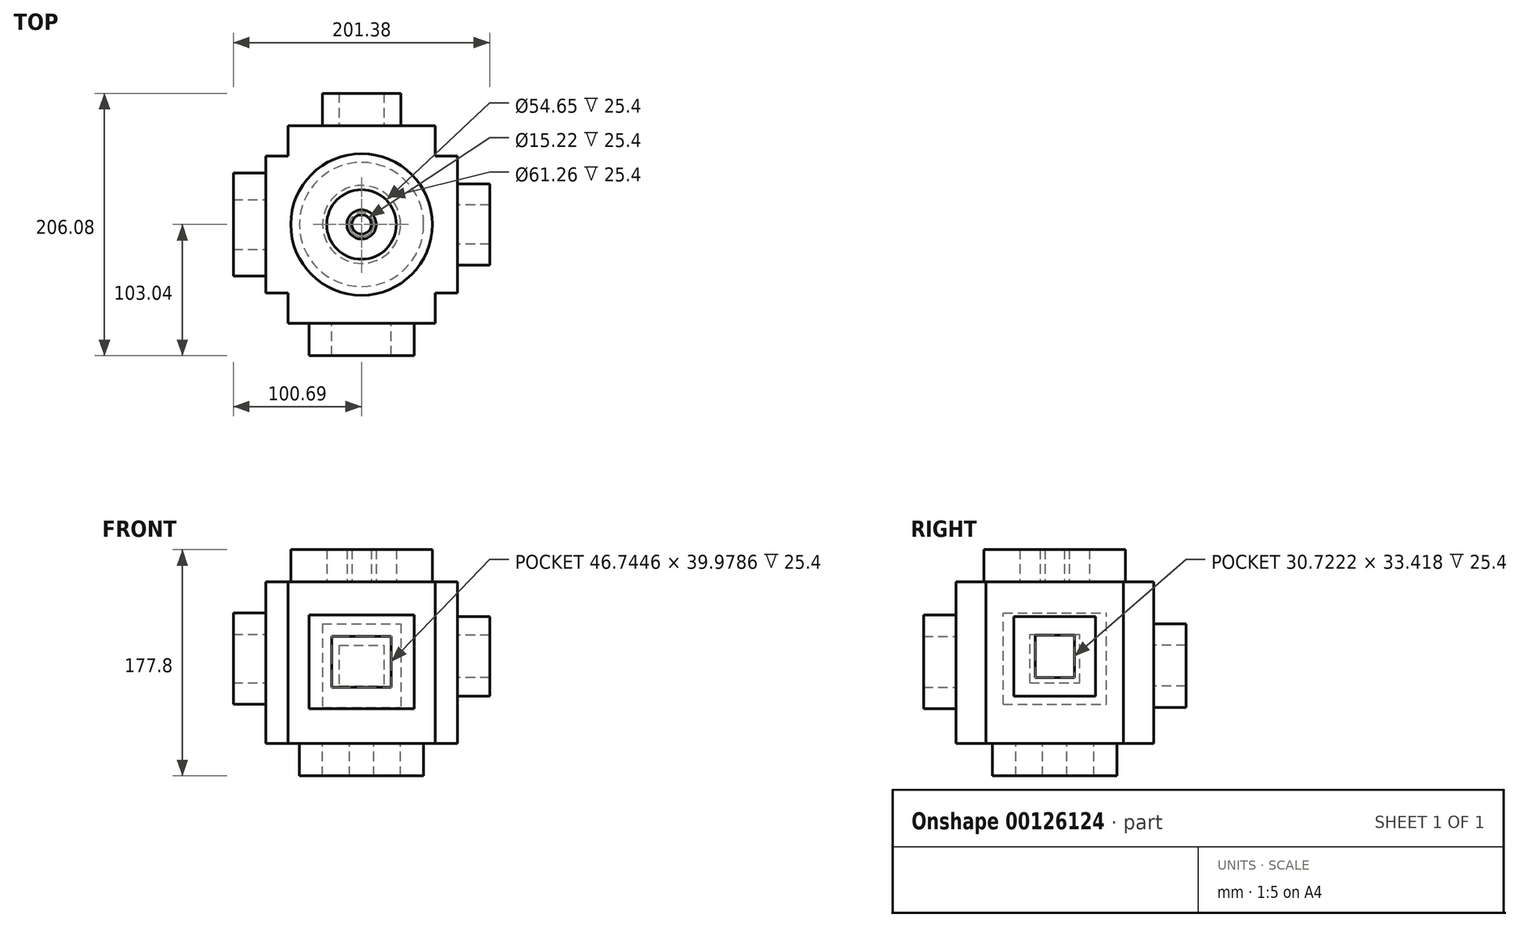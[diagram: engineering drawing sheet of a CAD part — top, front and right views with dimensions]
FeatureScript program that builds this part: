
annotation { "Feature Type Name" : "Feature", "Feature Type Description" : "" }
export const myFeature = defineFeature(function(context is Context, id is Id, definition is map)
    precondition{}
    {
        {
            var Q0;
            Q0=qCreatedBy(makeId("Top.planeOp"),FACE);
            var sketch = newSketch(context, id + "F0", { "sketchPlane" : qUnion([Q0])});
            skLineSegment(sketch, "E0.bottom", {"start": v(75.29, 53.92) * mm, "end": v(-75.29, 53.92) * mm});
            skLineSegment(sketch, "E0.top", {"start": v(75.29, -53.92) * mm, "end": v(-75.29, -53.92) * mm});
            skLineSegment(sketch, "E0.left", {"start": v(75.29, 53.92) * mm, "end": v(75.29, -53.92) * mm});
            skLineSegment(sketch, "E0.right", {"start": v(-75.29, 53.92) * mm, "end": v(-75.29, -53.92) * mm});
            skPoint(sketch, "E0.middle", {"position": v(0, 0) * mm});
            skLineSegment(sketch, "E1.bottom", {"start": v(57.75, 77.64) * mm, "end": v(-57.75, 77.64) * mm});
            skLineSegment(sketch, "E1.top", {"start": v(57.75, -77.64) * mm, "end": v(-57.75, -77.64) * mm});
            skLineSegment(sketch, "E1.left", {"start": v(57.75, 77.64) * mm, "end": v(57.75, -77.64) * mm});
            skLineSegment(sketch, "E1.right", {"start": v(-57.75, 77.64) * mm, "end": v(-57.75, -77.64) * mm});
            skSolve(sketch);
        }
        {
            var Q0;
            {var subQ0=sQuery(id+"F0.wireOp",EDGE,"E1.left");var subQ1=sQuery(id+"F0.wireOp",EDGE,"E0.bottom");var subQ2=makeQuery(id+"F0.imprint","INTERSECT",VERTEX,{"derivedFrom":[subQ1,subQ0]});Q0=makeQuery(id+"F0.imprint","IMPRINT",FACE,{"disambiguationData":[TD([[makeQuery(id+"F0.imprint","IMPRINT",EDGE,{"disambiguationData":[TD([[subQ2,-1.0]])],"derivedFrom":subQ1}),1.0]])]});}
            var Q1;
            {var subQ0=sQuery(id+"F0.wireOp",EDGE,"E0.right");Q1=makeQuery(id+"F0.imprint","IMPRINT",FACE,{"disambiguationData":[TD([[makeQuery(id+"F0.imprint","IMPRINT",EDGE,{"derivedFrom":subQ0}),1.0]])]});}
            var Q2;
            {var subQ5=sQuery(id+"F0.wireOp",EDGE,"E1.bottom");Q2=makeQuery(id+"F0.imprint","IMPRINT",FACE,{"disambiguationData":[TD([[makeQuery(id+"F0.imprint","IMPRINT",EDGE,{"derivedFrom":subQ5}),1.0]])]});}
            var Q3;
            {var subQ0=sQuery(id+"F0.wireOp",EDGE,"E0.left");Q3=makeQuery(id+"F0.imprint","IMPRINT",FACE,{"disambiguationData":[TD([[makeQuery(id+"F0.imprint","IMPRINT",EDGE,{"derivedFrom":subQ0}),-1.0]])]});}
            var Q4;
            {var subQ5=sQuery(id+"F0.wireOp",EDGE,"E1.top");Q4=makeQuery(id+"F0.imprint","IMPRINT",FACE,{"disambiguationData":[TD([[makeQuery(id+"F0.imprint","IMPRINT",EDGE,{"derivedFrom":subQ5}),-1.0]])]});}
            extrude(context, id + "F1", {"entities" : qUnion([Q0, Q1, Q2, Q3, Q4]), "depth" : 127 * mm});
        }
        {
            var Q0;
            Q0=makeQuery(id+"F1.opExtrude","CAP_FACE",FACE,{"disambiguationData":[OSD([sQuery(id+"F0.wireOp",EDGE,"E0.bottom"),sQuery(id+"F0.wireOp",EDGE,"E0.top"),sQuery(id+"F0.wireOp",EDGE,"E0.left"),sQuery(id+"F0.wireOp",EDGE,"E0.right"),sQuery(id+"F0.wireOp",EDGE,"E1.bottom"),sQuery(id+"F0.wireOp",EDGE,"E1.top"),sQuery(id+"F0.wireOp",EDGE,"E1.left"),sQuery(id+"F0.wireOp",EDGE,"E1.right")])],"isStart":false});
            var sketch = newSketch(context, id + "F2", { "sketchPlane" : qUnion([Q0])});
            skCircle(sketch, "E2", {"center": v(0, 0) * mm, "radius": 55.61 * mm});
            skCircle(sketch, "E3", {"center": v(0, 0) * mm, "radius": 60.45 * mm});
            skCircle(sketch, "E4", {"center": v(0, 0) * mm, "radius": 41.5 * mm});
            skCircle(sketch, "E5", {"center": v(0, 0) * mm, "radius": 27.33 * mm});
            skCircle(sketch, "E6", {"center": v(0, 0) * mm, "radius": 17.16 * mm});
            skCircle(sketch, "E7", {"center": v(0, 0) * mm, "radius": 11.49 * mm});
            skCircle(sketch, "E8", {"center": v(0, 0) * mm, "radius": 7.61 * mm});
            skSolve(sketch);
        }
        {
            var Q0;
            Q0=makeQuery(id+"F2.imprint","IMPRINT",FACE,{"disambiguationData":[TD([[makeQuery(id+"F2.imprint","IMPRINT",EDGE,{"derivedFrom":sQuery(id+"F2.wireOp",EDGE,"E2")}),1.0]])]});
            var Q1;
            Q1=makeQuery(id+"F2.imprint","IMPRINT",FACE,{"disambiguationData":[TD([[makeQuery(id+"F2.imprint","IMPRINT",EDGE,{"derivedFrom":sQuery(id+"F2.wireOp",EDGE,"E4")}),1.0]])]});
            var Q2;
            Q2=makeQuery(id+"F2.imprint","IMPRINT",FACE,{"disambiguationData":[TD([[makeQuery(id+"F2.imprint","IMPRINT",EDGE,{"derivedFrom":sQuery(id+"F2.wireOp",EDGE,"E7")}),1.0]])]});
            extrude(context, id + "F3", {"entities" : qUnion([Q0, Q1, Q2]), "operationType" : NewBodyOperationType.ADD, "depth" : 25.4 * mm});
        }
        {
            var Q0;
            Q0=makeQuery(id+"F1.opExtrude","SWEPT_FACE",FACE,{"disambiguationData":[OSD([sQuery(id+"F0.wireOp",EDGE,"E0.left")])]});
            var sketch = newSketch(context, id + "F4", { "sketchPlane" : qUnion([Q0])});
            skLineSegment(sketch, "E9.bottom", {"start": v(32.02, 37.27) * mm, "end": v(-32.02, 37.27) * mm});
            skLineSegment(sketch, "E9.top", {"start": v(32.02, 99.76) * mm, "end": v(-32.02, 99.76) * mm});
            skLineSegment(sketch, "E9.left", {"start": v(32.02, 37.27) * mm, "end": v(32.02, 99.76) * mm});
            skLineSegment(sketch, "E9.right", {"start": v(-32.02, 37.27) * mm, "end": v(-32.02, 99.76) * mm});
            skPoint(sketch, "E9.middle", {"position": v(0, 68.52) * mm});
            skLineSegment(sketch, "E10.bottom", {"start": v(15.36, 51.8) * mm, "end": v(-15.36, 51.8) * mm});
            skLineSegment(sketch, "E10.top", {"start": v(15.36, 85.23) * mm, "end": v(-15.36, 85.23) * mm});
            skLineSegment(sketch, "E10.left", {"start": v(15.36, 51.8) * mm, "end": v(15.36, 85.23) * mm});
            skLineSegment(sketch, "E10.right", {"start": v(-15.36, 51.8) * mm, "end": v(-15.36, 85.23) * mm});
            skSolve(sketch);
        }
        {
            var Q0;
            Q0=makeQuery(id+"F4.imprint","IMPRINT",FACE,{"disambiguationData":[TD([[makeQuery(id+"F4.imprint","IMPRINT",EDGE,{"derivedFrom":sQuery(id+"F4.wireOp",EDGE,"E9.bottom")}),-1.0]])]});
            extrude(context, id + "F5", {"entities" : qUnion([Q0]), "operationType" : NewBodyOperationType.ADD, "depth" : 25.4 * mm});
        }
        {
            var Q0;
            Q0=makeQuery(id+"F1.opExtrude","SWEPT_FACE",FACE,{"disambiguationData":[OSD([sQuery(id+"F0.wireOp",EDGE,"E1.bottom")])]});
            var sketch = newSketch(context, id + "F6", { "sketchPlane" : qUnion([Q0])});
            skLineSegment(sketch, "E11.bottom", {"start": v(30.84, 94.16) * mm, "end": v(-30.84, 94.16) * mm});
            skLineSegment(sketch, "E11.top", {"start": v(30.84, 28.22) * mm, "end": v(-30.84, 28.22) * mm});
            skLineSegment(sketch, "E11.left", {"start": v(30.84, 94.16) * mm, "end": v(30.84, 28.22) * mm});
            skLineSegment(sketch, "E11.right", {"start": v(-30.84, 94.16) * mm, "end": v(-30.84, 28.22) * mm});
            skPoint(sketch, "E11.middle", {"position": v(0, 61.2) * mm});
            skLineSegment(sketch, "E12.bottom", {"start": v(17.59, 77.27) * mm, "end": v(-17.59, 77.27) * mm});
            skLineSegment(sketch, "E12.top", {"start": v(17.59, 45.11) * mm, "end": v(-17.59, 45.11) * mm});
            skLineSegment(sketch, "E12.left", {"start": v(17.59, 77.27) * mm, "end": v(17.59, 45.11) * mm});
            skLineSegment(sketch, "E12.right", {"start": v(-17.59, 77.27) * mm, "end": v(-17.59, 45.11) * mm});
            skSolve(sketch);
        }
        {
            var Q0;
            Q0=makeQuery(id+"F6.imprint","IMPRINT",FACE,{"disambiguationData":[TD([[makeQuery(id+"F6.imprint","IMPRINT",EDGE,{"derivedFrom":sQuery(id+"F6.wireOp",EDGE,"E11.bottom")}),1.0]])]});
            extrude(context, id + "F7", {"entities" : qUnion([Q0]), "operationType" : NewBodyOperationType.ADD, "depth" : 25.4 * mm});
        }
        {
            var Q0;
            Q0=makeQuery(id+"F1.opExtrude","SWEPT_FACE",FACE,{"disambiguationData":[OSD([sQuery(id+"F0.wireOp",EDGE,"E1.top")])]});
            var sketch = newSketch(context, id + "F8", { "sketchPlane" : qUnion([Q0])});
            skLineSegment(sketch, "E13.bottom", {"start": v(41.33, 27.27) * mm, "end": v(-41.33, 27.27) * mm});
            skLineSegment(sketch, "E13.top", {"start": v(41.33, 100.92) * mm, "end": v(-41.33, 100.92) * mm});
            skLineSegment(sketch, "E13.left", {"start": v(41.33, 27.27) * mm, "end": v(41.33, 100.92) * mm});
            skLineSegment(sketch, "E13.right", {"start": v(-41.33, 27.27) * mm, "end": v(-41.33, 100.92) * mm});
            skPoint(sketch, "E13.middle", {"position": v(0, 64.1) * mm});
            skLineSegment(sketch, "E14.bottom", {"start": v(23.37, 44.1) * mm, "end": v(-23.37, 44.1) * mm});
            skLineSegment(sketch, "E14.top", {"start": v(23.37, 84.08) * mm, "end": v(-23.37, 84.08) * mm});
            skLineSegment(sketch, "E14.left", {"start": v(23.37, 44.1) * mm, "end": v(23.37, 84.08) * mm});
            skLineSegment(sketch, "E14.right", {"start": v(-23.37, 44.1) * mm, "end": v(-23.37, 84.08) * mm});
            skSolve(sketch);
        }
        {
            var Q0;
            Q0=makeQuery(id+"F8.imprint","IMPRINT",FACE,{"disambiguationData":[TD([[makeQuery(id+"F8.imprint","IMPRINT",EDGE,{"derivedFrom":sQuery(id+"F8.wireOp",EDGE,"E13.bottom")}),-1.0]])]});
            extrude(context, id + "F9", {"entities" : qUnion([Q0]), "operationType" : NewBodyOperationType.ADD, "depth" : 25.4 * mm});
        }
        {
            var Q0;
            Q0=makeQuery(id+"F1.opExtrude","SWEPT_FACE",FACE,{"disambiguationData":[OSD([sQuery(id+"F0.wireOp",EDGE,"E0.right")])]});
            var sketch = newSketch(context, id + "F10", { "sketchPlane" : qUnion([Q0])});
            skLineSegment(sketch, "E15.bottom", {"start": v(40.5, 30.74) * mm, "end": v(-40.5, 30.74) * mm});
            skLineSegment(sketch, "E15.top", {"start": v(40.5, 102.64) * mm, "end": v(-40.5, 102.64) * mm});
            skLineSegment(sketch, "E15.left", {"start": v(40.5, 30.74) * mm, "end": v(40.5, 102.64) * mm});
            skLineSegment(sketch, "E15.right", {"start": v(-40.5, 30.74) * mm, "end": v(-40.5, 102.64) * mm});
            skPoint(sketch, "E15.middle", {"position": v(0, 66.69) * mm});
            skLineSegment(sketch, "E16.bottom", {"start": v(19.52, 47.58) * mm, "end": v(-19.52, 47.58) * mm});
            skLineSegment(sketch, "E16.top", {"start": v(19.52, 85.8) * mm, "end": v(-19.52, 85.8) * mm});
            skLineSegment(sketch, "E16.left", {"start": v(19.52, 47.58) * mm, "end": v(19.52, 85.8) * mm});
            skLineSegment(sketch, "E16.right", {"start": v(-19.52, 47.58) * mm, "end": v(-19.52, 85.8) * mm});
            skSolve(sketch);
        }
        {
            var Q0;
            Q0=makeQuery(id+"F10.imprint","IMPRINT",FACE,{"disambiguationData":[TD([[makeQuery(id+"F10.imprint","IMPRINT",EDGE,{"derivedFrom":sQuery(id+"F10.wireOp",EDGE,"E15.bottom")}),-1.0]])]});
            extrude(context, id + "F11", {"entities" : qUnion([Q0]), "operationType" : NewBodyOperationType.ADD, "depth" : 25.4 * mm});
        }
        {
            var Q0;
            Q0=makeQuery(id+"F1.opExtrude","CAP_FACE",FACE,{"disambiguationData":[OSD([sQuery(id+"F0.wireOp",EDGE,"E0.bottom"),sQuery(id+"F0.wireOp",EDGE,"E0.top"),sQuery(id+"F0.wireOp",EDGE,"E0.left"),sQuery(id+"F0.wireOp",EDGE,"E0.right"),sQuery(id+"F0.wireOp",EDGE,"E1.bottom"),sQuery(id+"F0.wireOp",EDGE,"E1.top"),sQuery(id+"F0.wireOp",EDGE,"E1.left"),sQuery(id+"F0.wireOp",EDGE,"E1.right")])],"isStart":true});
            var sketch = newSketch(context, id + "F12", { "sketchPlane" : qUnion([Q0])});
            skCircle(sketch, "E17", {"center": v(0, 0) * mm, "radius": 67.55 * mm});
            skCircle(sketch, "E18", {"center": v(0, 0) * mm, "radius": 48.81 * mm});
            skCircle(sketch, "E19", {"center": v(0, 0) * mm, "radius": 30.63 * mm});
            skCircle(sketch, "E20", {"center": v(0, 0) * mm, "radius": 15.43 * mm});
            skCircle(sketch, "E21", {"center": v(0, 0) * mm, "radius": 9.56 * mm});
            skSolve(sketch);
        }
        {
            var Q0;
            Q0=makeQuery(id+"F12.imprint","IMPRINT",FACE,{"disambiguationData":[TD([[makeQuery(id+"F12.imprint","IMPRINT",EDGE,{"derivedFrom":sQuery(id+"F12.wireOp",EDGE,"E18")}),1.0]])]});
            var Q1;
            Q1=makeQuery(id+"F12.imprint","IMPRINT",FACE,{"disambiguationData":[TD([[makeQuery(id+"F12.imprint","IMPRINT",EDGE,{"derivedFrom":sQuery(id+"F12.wireOp",EDGE,"E21")}),1.0]])]});
            extrude(context, id + "F13", {"entities" : qUnion([Q0, Q1]), "operationType" : NewBodyOperationType.ADD, "depth" : 25.4 * mm});
        }
    });
